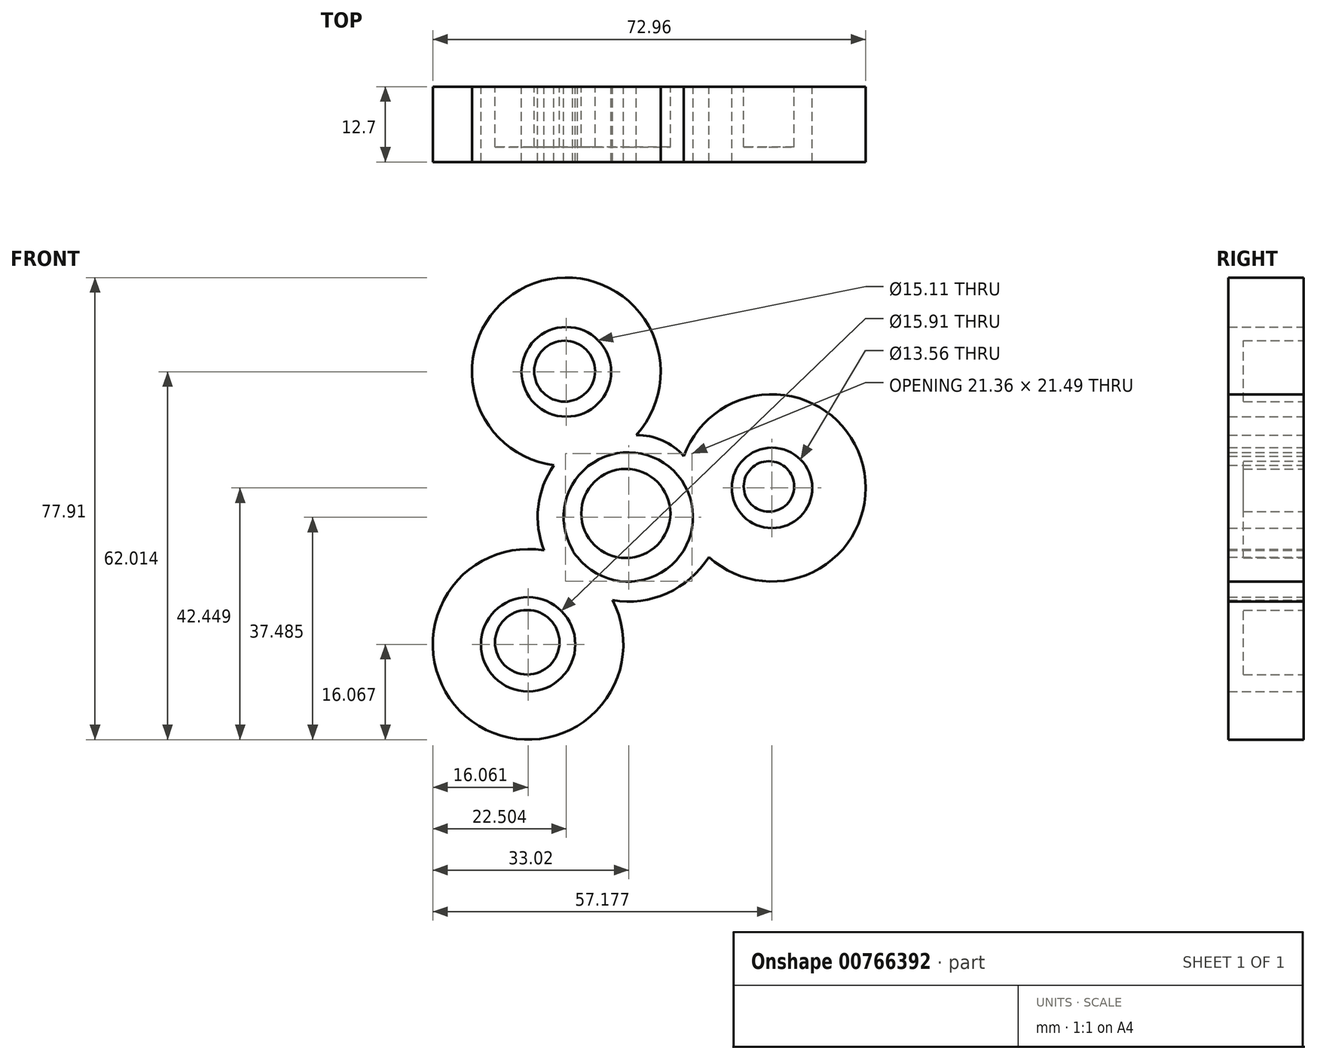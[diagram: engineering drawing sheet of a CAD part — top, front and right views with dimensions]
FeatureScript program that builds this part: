
annotation { "Feature Type Name" : "Feature", "Feature Type Description" : "" }
export const myFeature = defineFeature(function(context is Context, id is Id, definition is map)
    precondition{}
    {
        {
            var Q0;
            Q0=qCreatedBy(makeId("Front.planeOp"),FACE);
            var sketch = newSketch(context, id + "F0", { "sketchPlane" : qUnion([Q0])});
            skCircle(sketch, "E0", {"center": v(-67.66, 41) * mm, "radius": 15.9 * mm});
            skCircle(sketch, "E1", {"center": v(-74.1, -4.94) * mm, "radius": 16.06 * mm});
            skCircle(sketch, "E2", {"center": v(-32.98, 21.44) * mm, "radius": 15.79 * mm});
            skArc(sketch, "E3", {"start": v(-69.77, 25.25) * mm, "mid": v(-72.4, 18.28) * mm, "end": v(-71.41, 10.9) * mm});
            skCircle(sketch, "E4", {"center": v(-57.21, 16.54) * mm, "radius": 10.9 * mm});
            skCircle(sketch, "E5", {"center": v(-64.26, 16.54) * mm, "radius": 2.36 * mm});
            skCircle(sketch, "E6", {"center": v(-64.26, 11.7) * mm, "radius": 2.45 * mm});
            skCircle(sketch, "E7", {"center": v(-57.21, 10.41) * mm, "radius": 2.48 * mm});
            skCircle(sketch, "E8", {"center": v(-54.8, 21.3) * mm, "radius": 3.93 * mm});
            skCircle(sketch, "E9", {"center": v(-60.2, 21.3) * mm, "radius": 3.23 * mm});
            skArc(sketch, "E10", {"start": v(-59.86, 2.5) * mm, "mid": v(-50.64, 3.68) * mm, "end": v(-43.64, 9.8) * mm});
            skArc(sketch, "E11", {"start": v(-47.84, 26.78) * mm, "mid": v(-51.46, 29.44) * mm, "end": v(-55.86, 30.35) * mm});
            skCircle(sketch, "E12", {"center": v(-67.66, 41) * mm, "radius": 7.56 * mm});
            skCircle(sketch, "E13", {"center": v(-32.98, 21.44) * mm, "radius": 6.78 * mm});
            skCircle(sketch, "E14", {"center": v(-74.1, -4.94) * mm, "radius": 7.95 * mm});
            skSolve(sketch);
        }
        {
            var Q0;
            Q0 = qSketchRegion(id + "F0", true);
            extrude(context, id + "F1", {"entities" : qUnion([Q0]), "depth" : 12.7 * mm, "offsetDistance" : 25.4 * mm});
        }
        {
            var Q0;
            Q0=qCreatedBy(makeId("Front.planeOp"),FACE);
            var sketch = newSketch(context, id + "F2", { "sketchPlane" : qUnion([Q0])});
            skCircle(sketch, "E15", {"center": v(-57.62, 17.13) * mm, "radius": 7.52 * mm});
            skCircle(sketch, "E16", {"center": v(-33.5, 21.69) * mm, "radius": 4.26 * mm});
            skCircle(sketch, "E17", {"center": v(-67.95, 41.13) * mm, "radius": 5.13 * mm});
            skCircle(sketch, "E18", {"center": v(-74.25, -4.6) * mm, "radius": 5.43 * mm});
            skSolve(sketch);
        }
        {
            var Q0;
            Q0=makeQuery(id+"F2.imprint","IMPRINT",FACE,{"disambiguationData":[TD([[makeQuery(id+"F2.imprint","IMPRINT",EDGE,{"derivedFrom":sQuery(id+"F2.wireOp",EDGE,"E15")}),1.0]])]});
            extrude(context, id + "F3", {"entities" : qUnion([Q0]), "depth" : 10.16 * mm, "offsetDistance" : 25.4 * mm});
        }
        {
            var Q0;
            Q0 = qSketchRegion(id + "F2", true);
            extrude(context, id + "F4", {"entities" : qUnion([Q0]), "operationType" : NewBodyOperationType.ADD, "depth" : 10.16 * mm, "offsetDistance" : 25.4 * mm});
        }
    });
